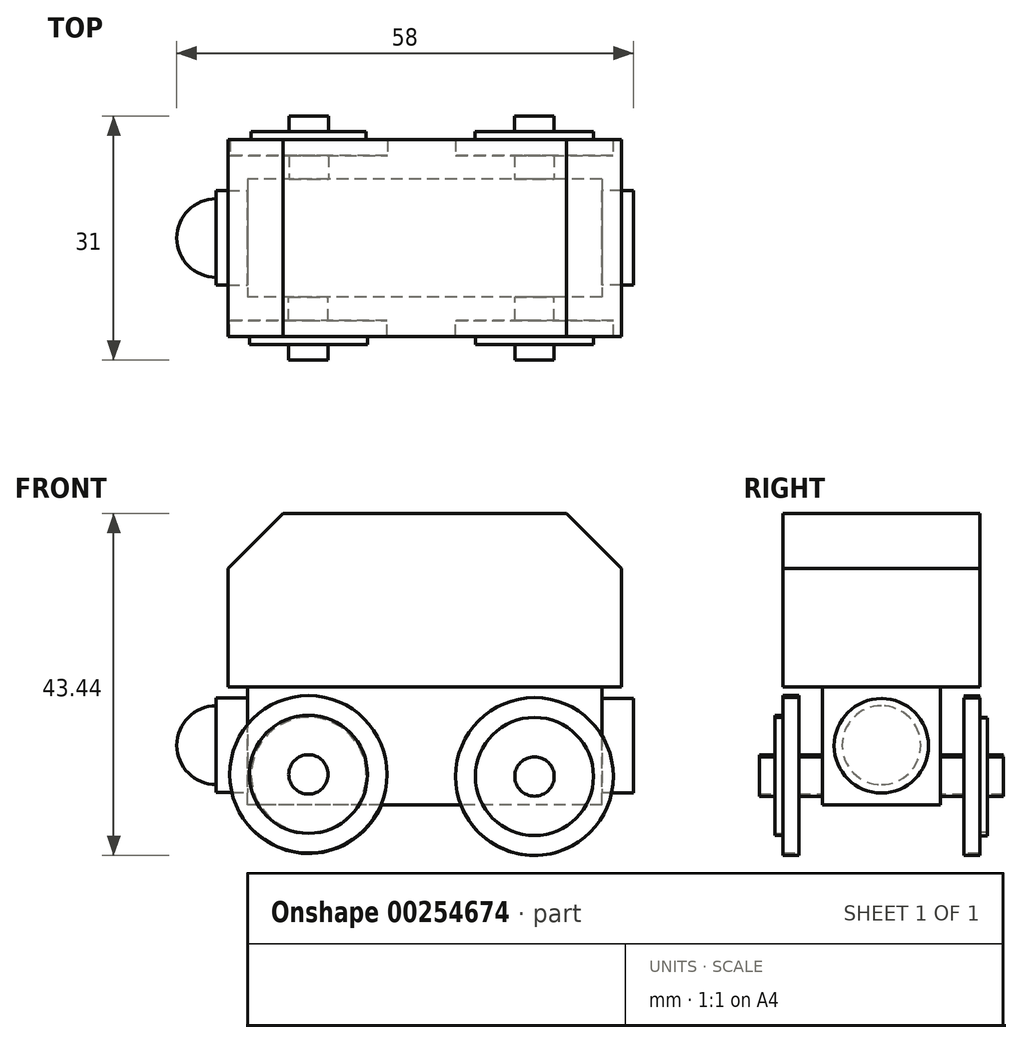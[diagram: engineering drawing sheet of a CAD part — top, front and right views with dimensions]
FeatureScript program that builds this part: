
annotation { "Feature Type Name" : "Feature", "Feature Type Description" : "" }
export const myFeature = defineFeature(function(context is Context, id is Id, definition is map)
    precondition{}
    {
        {
            var Q0;
            Q0=qCreatedBy(makeId("Front.planeOp"),FACE);
            var sketch = newSketch(context, id + "F0", { "sketchPlane" : qUnion([Q0])});
            skLineSegment(sketch, "E0.bottom", {"start": v(25, -11) * mm, "end": v(-25, -11) * mm});
            skLineSegment(sketch, "E0.top", {"start": v(25, 11) * mm, "end": v(-25, 11) * mm});
            skLineSegment(sketch, "E0.left", {"start": v(25, -11) * mm, "end": v(25, 11) * mm});
            skLineSegment(sketch, "E0.right", {"start": v(-25, -11) * mm, "end": v(-25, 11) * mm});
            skPoint(sketch, "E0.middle", {"position": v(0, 0) * mm});
            skSolve(sketch);
        }
        {
            var Q0;
            Q0 = qSketchRegion(id + "F0", true);
            extrude(context, id + "F1", {"entities" : qUnion([Q0]), "endBound" : BoundingType.SYMMETRIC, "depth" : 25 * mm});
        }
        {
            var Q0;
            Q0=makeQuery(id+"F1.opExtrude","SWEPT_FACE",FACE,{"disambiguationData":[OSD([sQuery(id+"F0.wireOp",EDGE,"E0.bottom")])]});
            var sketch = newSketch(context, id + "F2", { "sketchPlane" : qUnion([Q0])});
            skLineSegment(sketch, "E1.bottom", {"start": v(22.5, -7.5) * mm, "end": v(-22.5, -7.5) * mm});
            skLineSegment(sketch, "E1.top", {"start": v(22.5, 7.5) * mm, "end": v(-22.5, 7.5) * mm});
            skLineSegment(sketch, "E1.left", {"start": v(22.5, -7.5) * mm, "end": v(22.5, 7.5) * mm});
            skLineSegment(sketch, "E1.right", {"start": v(-22.5, -7.5) * mm, "end": v(-22.5, 7.5) * mm});
            skPoint(sketch, "E1.middle", {"position": v(0, 0) * mm});
            skSolve(sketch);
        }
        {
            var Q0;
            Q0=makeQuery(id+"F2.imprint","IMPRINT",FACE,{"disambiguationData":[TD([[makeQuery(id+"F2.imprint","IMPRINT",EDGE,{"derivedFrom":sQuery(id+"F2.wireOp",EDGE,"E1.bottom")}),-1.0]])]});
            extrude(context, id + "F3", {"entities" : qUnion([Q0]), "operationType" : NewBodyOperationType.ADD, "depth" : 15 * mm});
        }
        {
            var Q0;
            Q0=makeQuery(id+"F3.opExtrude","SWEPT_FACE",FACE,{"disambiguationData":[OSD([sQuery(id+"F2.wireOp",EDGE,"E1.top")])]});
            var sketch = newSketch(context, id + "F4", { "sketchPlane" : qUnion([Q0])});
            skCircle(sketch, "E2", {"center": v(13.93, -22.4) * mm, "radius": 2.5 * mm});
            skSolve(sketch);
        }
        {
            var Q0;
            Q0 = qSketchRegion(id + "F4", true);
            extrude(context, id + "F5", {"entities" : qUnion([Q0]), "operationType" : NewBodyOperationType.ADD, "depth" : 3 * mm});
        }
        {
            var Q0;
            Q0=makeQuery(id+"F3.opExtrude","SWEPT_FACE",FACE,{"disambiguationData":[OSD([sQuery(id+"F2.wireOp",EDGE,"E1.top")])]});
            var sketch = newSketch(context, id + "F6", { "sketchPlane" : qUnion([Q0])});
            skCircle(sketch, "E3", {"center": v(-14.78, -22.14) * mm, "radius": 2.5 * mm});
            skSolve(sketch);
        }
        {
            var Q0;
            Q0 = qSketchRegion(id + "F6", true);
            extrude(context, id + "F7", {"entities" : qUnion([Q0]), "operationType" : NewBodyOperationType.ADD, "depth" : 3 * mm});
        }
        {
            var Q0;
            Q0=makeQuery(id+"F3.opExtrude","SWEPT_FACE",FACE,{"disambiguationData":[OSD([sQuery(id+"F2.wireOp",EDGE,"E1.bottom")])]});
            var sketch = newSketch(context, id + "F8", { "sketchPlane" : qUnion([Q0])});
            skCircle(sketch, "E4", {"center": v(14.74, -22.19) * mm, "radius": 2.5 * mm});
            skSolve(sketch);
        }
        {
            var Q0;
            Q0 = qSketchRegion(id + "F8", true);
            extrude(context, id + "F9", {"entities" : qUnion([Q0]), "operationType" : NewBodyOperationType.ADD, "depth" : 3 * mm});
        }
        {
            var Q0;
            Q0=makeQuery(id+"F3.opExtrude","SWEPT_FACE",FACE,{"disambiguationData":[OSD([sQuery(id+"F2.wireOp",EDGE,"E1.bottom")])]});
            var sketch = newSketch(context, id + "F10", { "sketchPlane" : qUnion([Q0])});
            skCircle(sketch, "E5", {"center": v(-13.9, -22.44) * mm, "radius": 2.5 * mm});
            skSolve(sketch);
        }
        {
            var Q0;
            Q0 = qSketchRegion(id + "F10", true);
            extrude(context, id + "F11", {"entities" : qUnion([Q0]), "operationType" : NewBodyOperationType.ADD, "depth" : 3 * mm});
        }
        {
            var Q0;
            Q0=makeQuery(id+"F11.opExtrude","CAP_FACE",FACE,{"disambiguationData":[OSD([sQuery(id+"F10.wireOp",EDGE,"E5")])],"isStart":false});
            var sketch = newSketch(context, id + "F12", { "sketchPlane" : qUnion([Q0])});
            skCircle(sketch, "E6", {"center": v(-13.9, -22.44) * mm, "radius": 10 * mm});
            skSolve(sketch);
        }
        {
            var Q0;
            Q0 = qSketchRegion(id + "F12", true);
            extrude(context, id + "F13", {"entities" : qUnion([Q0]), "operationType" : NewBodyOperationType.ADD, "depth" : 2 * mm});
        }
        {
            var Q0;
            Q0=makeQuery(id+"F9.opExtrude","CAP_FACE",FACE,{"disambiguationData":[OSD([sQuery(id+"F8.wireOp",EDGE,"E4")])],"isStart":false});
            var sketch = newSketch(context, id + "F14", { "sketchPlane" : qUnion([Q0])});
            skCircle(sketch, "E7", {"center": v(14.74, -22.19) * mm, "radius": 10 * mm});
            skSolve(sketch);
        }
        {
            var Q0;
            Q0 = qSketchRegion(id + "F14", true);
            extrude(context, id + "F15", {"entities" : qUnion([Q0]), "operationType" : NewBodyOperationType.ADD, "depth" : 2 * mm});
        }
        {
            var Q0;
            Q0=makeQuery(id+"F7.opExtrude","CAP_FACE",FACE,{"disambiguationData":[OSD([sQuery(id+"F6.wireOp",EDGE,"E3")])],"isStart":false});
            var sketch = newSketch(context, id + "F16", { "sketchPlane" : qUnion([Q0])});
            skCircle(sketch, "E8", {"center": v(-14.78, -22.14) * mm, "radius": 10 * mm});
            skSolve(sketch);
        }
        {
            var Q0;
            Q0 = qSketchRegion(id + "F16", true);
            extrude(context, id + "F17", {"entities" : qUnion([Q0]), "operationType" : NewBodyOperationType.ADD, "depth" : 2 * mm});
        }
        {
            var Q0;
            Q0=makeQuery(id+"F5.opExtrude","CAP_FACE",FACE,{"disambiguationData":[OSD([sQuery(id+"F4.wireOp",EDGE,"E2")])],"isStart":false});
            var sketch = newSketch(context, id + "F18", { "sketchPlane" : qUnion([Q0])});
            skCircle(sketch, "E9", {"center": v(13.93, -22.4) * mm, "radius": 10.01 * mm});
            skSolve(sketch);
        }
        {
            var Q0;
            Q0 = qSketchRegion(id + "F18", true);
            extrude(context, id + "F19", {"entities" : qUnion([Q0]), "operationType" : NewBodyOperationType.ADD, "depth" : 2 * mm});
        }
        {
            var Q0;
            Q0=makeQuery(id+"F17.opExtrude","CAP_FACE",FACE,{"disambiguationData":[OSD([sQuery(id+"F16.wireOp",EDGE,"E8")])],"isStart":false});
            var sketch = newSketch(context, id + "F20", { "sketchPlane" : qUnion([Q0])});
            skCircle(sketch, "E10", {"center": v(-14.78, -22.14) * mm, "radius": 7.5 * mm});
            skSolve(sketch);
        }
        {
            var Q0;
            Q0 = qSketchRegion(id + "F20", true);
            extrude(context, id + "F21", {"entities" : qUnion([Q0]), "operationType" : NewBodyOperationType.ADD, "depth" : 1 * mm});
        }
        {
            var Q0;
            Q0=makeQuery(id+"F19.opExtrude","CAP_FACE",FACE,{"disambiguationData":[OSD([sQuery(id+"F18.wireOp",EDGE,"E9")])],"isStart":false});
            var sketch = newSketch(context, id + "F22", { "sketchPlane" : qUnion([Q0])});
            skCircle(sketch, "E11", {"center": v(13.93, -22.4) * mm, "radius": 7.5 * mm});
            skSolve(sketch);
        }
        {
            var Q0;
            Q0=makeQuery(id+"F22.imprint","IMPRINT",FACE,{"disambiguationData":[TD([[makeQuery(id+"F22.imprint","IMPRINT",EDGE,{"derivedFrom":sQuery(id+"F22.wireOp",EDGE,"E11")}),1.0]])]});
            extrude(context, id + "F23", {"entities" : qUnion([Q0]), "operationType" : NewBodyOperationType.ADD, "depth" : 1 * mm});
        }
        {
            var Q0;
            Q0=makeQuery(id+"F13.opExtrude","CAP_FACE",FACE,{"disambiguationData":[OSD([sQuery(id+"F12.wireOp",EDGE,"E6")])],"isStart":false});
            var sketch = newSketch(context, id + "F24", { "sketchPlane" : qUnion([Q0])});
            skCircle(sketch, "E12", {"center": v(-13.9, -22.44) * mm, "radius": 7.5 * mm});
            skSolve(sketch);
        }
        {
            var Q0;
            Q0 = qSketchRegion(id + "F24", true);
            extrude(context, id + "F25", {"entities" : qUnion([Q0]), "operationType" : NewBodyOperationType.ADD, "depth" : 1 * mm});
        }
        {
            var Q0;
            Q0=makeQuery(id+"F15.opExtrude","CAP_FACE",FACE,{"disambiguationData":[OSD([sQuery(id+"F14.wireOp",EDGE,"E7")])],"isStart":false});
            var sketch = newSketch(context, id + "F26", { "sketchPlane" : qUnion([Q0])});
            skCircle(sketch, "E13", {"center": v(14.74, -22.19) * mm, "radius": 7.3 * mm});
            skSolve(sketch);
        }
        {
            var Q0;
            Q0 = qSketchRegion(id + "F26", true);
            extrude(context, id + "F27", {"entities" : qUnion([Q0]), "operationType" : NewBodyOperationType.ADD, "depth" : 1 * mm});
        }
        {
            var Q0;
            Q0=makeQuery(id+"F25.opExtrude","CAP_FACE",FACE,{"disambiguationData":[OSD([sQuery(id+"F24.wireOp",EDGE,"E12")])],"isStart":false});
            var sketch = newSketch(context, id + "F28", { "sketchPlane" : qUnion([Q0])});
            skCircle(sketch, "E14", {"center": v(-13.9, -22.44) * mm, "radius": 2.5 * mm});
            skSolve(sketch);
        }
        {
            var Q0;
            Q0 = qSketchRegion(id + "F28", true);
            extrude(context, id + "F29", {"entities" : qUnion([Q0]), "operationType" : NewBodyOperationType.ADD, "depth" : 2 * mm});
        }
        {
            var Q0;
            Q0=makeQuery(id+"F27.opExtrude","CAP_FACE",FACE,{"disambiguationData":[OSD([sQuery(id+"F26.wireOp",EDGE,"E13")])],"isStart":false});
            var sketch = newSketch(context, id + "F30", { "sketchPlane" : qUnion([Q0])});
            skCircle(sketch, "E15", {"center": v(14.74, -22.19) * mm, "radius": 2.5 * mm});
            skSolve(sketch);
        }
        {
            var Q0;
            Q0 = qSketchRegion(id + "F30", true);
            extrude(context, id + "F31", {"entities" : qUnion([Q0]), "operationType" : NewBodyOperationType.ADD, "depth" : 2 * mm});
        }
        {
            var Q0;
            Q0=makeQuery(id+"F21.opExtrude","CAP_FACE",FACE,{"disambiguationData":[OSD([sQuery(id+"F20.wireOp",EDGE,"E10")])],"isStart":false});
            var sketch = newSketch(context, id + "F32", { "sketchPlane" : qUnion([Q0])});
            skCircle(sketch, "E16", {"center": v(-14.78, -22.14) * mm, "radius": 2.5 * mm});
            skSolve(sketch);
        }
        {
            var Q0;
            Q0 = qSketchRegion(id + "F32", true);
            extrude(context, id + "F33", {"entities" : qUnion([Q0]), "operationType" : NewBodyOperationType.ADD, "depth" : 2 * mm});
        }
        {
            var Q0;
            Q0=makeQuery(id+"F23.opExtrude","CAP_FACE",FACE,{"disambiguationData":[OSD([sQuery(id+"F22.wireOp",EDGE,"E11")])],"isStart":false});
            var sketch = newSketch(context, id + "F34", { "sketchPlane" : qUnion([Q0])});
            skCircle(sketch, "E17", {"center": v(13.93, -22.4) * mm, "radius": 2.5 * mm});
            skSolve(sketch);
        }
        {
            var Q0;
            Q0 = qSketchRegion(id + "F34", true);
            extrude(context, id + "F35", {"entities" : qUnion([Q0]), "operationType" : NewBodyOperationType.ADD, "depth" : 2 * mm});
        }
        {
            var Q0;
            Q0=makeQuery(id+"F3.opExtrude","SWEPT_FACE",FACE,{"disambiguationData":[OSD([sQuery(id+"F2.wireOp",EDGE,"E1.right")])]});
            var sketch = newSketch(context, id + "F36", { "sketchPlane" : qUnion([Q0])});
            skCircle(sketch, "E18", {"center": v(0, -18.44) * mm, "radius": 6 * mm});
            skSolve(sketch);
        }
        {
            var Q0;
            Q0 = qSketchRegion(id + "F36", true);
            extrude(context, id + "F37", {"entities" : qUnion([Q0]), "operationType" : NewBodyOperationType.ADD, "depth" : 4 * mm});
        }
        {
            var Q0;
            Q0=makeQuery(id+"F3.opExtrude","SWEPT_FACE",FACE,{"disambiguationData":[OSD([sQuery(id+"F2.wireOp",EDGE,"E1.left")])]});
            var sketch = newSketch(context, id + "F38", { "sketchPlane" : qUnion([Q0])});
            skCircle(sketch, "E19", {"center": v(0, -18.5) * mm, "radius": 6 * mm});
            skSolve(sketch);
        }
        {
            var Q0;
            Q0 = qSketchRegion(id + "F38", true);
            extrude(context, id + "F39", {"entities" : qUnion([Q0]), "operationType" : NewBodyOperationType.ADD, "depth" : 4 * mm});
        }
        {
            var Q0;
            Q0=makeQuery(id+"F37.opExtrude","CAP_FACE",FACE,{"disambiguationData":[OSD([sQuery(id+"F36.wireOp",EDGE,"E18")])],"isStart":false});
            var sketch = newSketch(context, id + "F40", { "sketchPlane" : qUnion([Q0])});
            skPoint(sketch, "E20", {"position": v(0, -18.44) * mm});
            skArc(sketch, "E21", {"start": v(0, -13.44) * mm, "mid": v(-5, -18.44) * mm, "end": v(0, -23.44) * mm});
            skLineSegment(sketch, "E22", {"start": v(0, -13.44) * mm, "end": v(0, -23.44) * mm});
            skSolve(sketch);
        }
        {
            var Q0;
            Q0=makeQuery(id+"F40.imprint","IMPRINT",FACE,{"disambiguationData":[TD([[makeQuery(id+"F40.imprint","IMPRINT",EDGE,{"derivedFrom":sQuery(id+"F40.wireOp",EDGE,"E21")}),1.0]])]});
            var Q1;
            Q1=sQuery(id+"F40.wireOp",EDGE,"E22");
            revolve(context, id + "F41", {"operationType" : NewBodyOperationType.ADD, "entities" : qUnion([Q0]), "axis" : qUnion([Q1]), "revolveType" : RevolveType.FULL});
        }
        {
            var Q0;
            Q0=makeQuery(id+"F1.opExtrude","SWEPT_EDGE",EDGE,{"disambiguationData":[OSD([sQuery(id+"F0.wireOp",EDGE,"E0.top"),sQuery(id+"F0.wireOp",EDGE,"E0.right")])]});
            chamfer(context, id + "F42", {"entities" : qUnion([Q0]), "width" : 7 * mm, "tangentPropagation" : true});
        }
        {
            var Q0;
            Q0=makeQuery(id+"F1.opExtrude","SWEPT_EDGE",EDGE,{"disambiguationData":[OSD([sQuery(id+"F0.wireOp",EDGE,"E0.top"),sQuery(id+"F0.wireOp",EDGE,"E0.left")])]});
            chamfer(context, id + "F43", {"entities" : qUnion([Q0]), "width" : 7 * mm, "tangentPropagation" : true});
        }
    });
